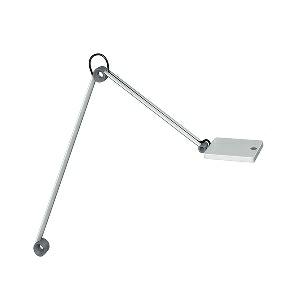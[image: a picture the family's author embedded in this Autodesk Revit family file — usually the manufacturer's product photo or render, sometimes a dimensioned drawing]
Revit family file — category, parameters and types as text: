
# Revit family: para_mi_-_ftl_108_r__930_00644082_7c1b
name_source: partatom
category: Lighting Fixtures
units: mm (PartAtom-declared; Revit-internal decimal feet)

## family parameters
Cut with Voids When Loaded = No
Host = Face
Light Source = No
Part Type = Normal
Room Calculation Point = No
Round Connector Dimension = Use Diameter
Shared = No

## types (1)
- PARA.MI - FTL 108 R /930 (1 x LED, 580 lm, 3000K)
    Apparent Load = 7 VA
    Approval mark = CE
    CIE Flux Codes = 70 94 99 100 100
    Color Rendering = 90-100
    Color Temperature = 3000K
    Control Gear = Electronic ballast
    Default Elevation = 1800 mm
    Description = FTL 108 R|Task luminaire|light source: LED|work equipment: Electronic plug-in transformer|connected load: 100-240 V, 50/60 Hz|Power consumption: approx. 7 W|luminous flux: 580 lm|luminous efficacy: 82 lm/W|Illuminance efficiency factor: 107 lx/W|colour temperature: Warm white, ca. 3000 K|color rendering index (CRI): >= 90|chromaticity tolerance:  3 SDCM|class of protection: II with plug-in power supply, III without plug-in power supply|technology: Continuously dimmable|luminaire body|material: Aluminium|surface: Painted|colour: Silver|lamp cover: Plastic, Clear|tubular sections|material: Tubular aluminium section|surface: Painted|colour: Silver metallic|weight (net): approx. 1.0 kg|mains lead: 3.00 m Mains plug BS 1363, CEE 7/XVI, NEMA 1-15P|Fastening: Adaptor (accessory), Table base (accessory), Table clamp (accessory), Tap16|glare control: Reflector|special features: Automatic switchoff adjustable, Push button in luminaire head, Behaviour at net recovery adjustable|Approval mark: C - ETL - US (F. CAN U. USA), VDE - ENEC SEP LIGHT & POWER SUPPLY UNIT|
    Height = 12 mm  [stored 0.0393701 ft]
    Lamp = 1 x LED
    Lamp Light Flux = 580 lm
    Lamp count = 1
    Length = 123 mm
    Luminous efficacy = 83 lm/W
    Manufacturer = Waldmann
    ModVariant = No
    Model = 00644082
    Mounting Place = Table
    Mounting Type = Surface mounted
    Number of Poles = 1
    OnlyDefault = Yes
    Power Factor = 1
    Product Name = PARA.MI - FTL 108 R /930
    Product group = Task luminaire (office)
    ProductGroupID = 21
    Protection Class = Protection class II
    Protection Degree = IP 40
    RLX_Detail_Level = 1
    RLX_Emergency_Light_Flux = 0 lm
    RLX_Emergency_Type = 0
    RLX_Emergency_Type_DB = No
    RlxData = <blob elided: 70365 chars, md5=c5e99599>
    Socket = socket
    Standby Power = 0 W
    System Light Flux = 580 lm
    System Power = 7 W
    Type Comments = Product without accessories
    Type Image = 113148000-00644097.jpg
    URL = http://relux.com
    VarID = ---
    Voltage = 230 V
    Voltage Range = 220-240 V
    Weight = 0.00 kg
    Width = 0 mm  [stored 0 ft]

note: [stored X ft] marks values corroborated as IEEE doubles in the binary element streams (Revit-internal decimal feet)

## geometry (parser evidence)
native form markers: Blend x4, Sweep x15
no freeform markers — native parametric forms only
